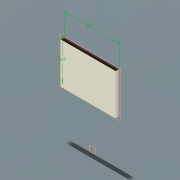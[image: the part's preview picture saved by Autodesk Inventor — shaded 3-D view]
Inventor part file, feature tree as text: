
AUTODESK INVENTOR PART (.ipt)
format: ipt  version: 2022 (Build 260153070, 153G)  size: 100,352 bytes
history: native  units: mm
features: other x3, sketch x1, extrude x1
ambient origin geometry x8: Origin, YZ Plane, XZ Plane, XY Plane, X Axis, Y Axis, Z Axis, Center Point
bodies: Body1 (feature_tree)
feature tree (5):
  other  "Твердое тело1"
  other  "РабПлоскость5"
  sketch  "Эскиз1"
  extrude  "Выдавливание1"  Depth=16.0mm TaperAngle=0.0deg
  other  "РабПлоскость6"
